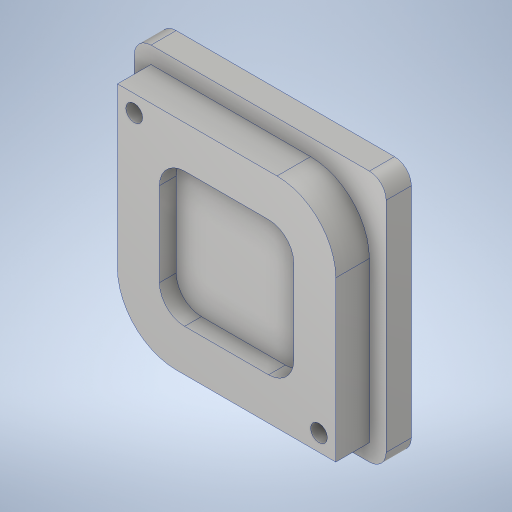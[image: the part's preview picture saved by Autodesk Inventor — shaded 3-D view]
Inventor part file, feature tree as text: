
AUTODESK INVENTOR PART (.ipt)
format: ipt  version: 2024 (Build 280153000, 153)  size: 330,752 bytes
history: native  units: in
note: dims shown in document units (in); Inventor stores cm internally (conversion verified against a paired STEP export)
features: sketch x5, thread x4, extrude x3, fillet x3, hole x2
ambient origin geometry x8: Origin, YZ Plane, XZ Plane, XY Plane, X Axis, Y Axis, Z Axis, Center Point
bodies: Solid1 (feature_tree)
feature tree (17):
  extrude  "Extrusion1"  Depth=3.75in
  extrude  "Extrusion2"  Depth=3.25in
  extrude  "Extrusion3"  Depth=0.5in TaperAngle=0.0deg
  hole  "Hole1"  [1 undecoded]
  hole  "Hole2"  [1 undecoded]
  fillet  "Fillet1"  Radius=0.25in
  fillet  "Fillet3"  Radius=0.25in
  fillet  "Fillet4"  Radius=0.25in
  thread  "Thread1"  [1 undecoded]
  thread  "Thread2"  [1 undecoded]
  thread  "Thread3"  [1 undecoded]
  thread  "Thread4"  [1 undecoded]
  sketch  "Sketch1"  dims[d0=3.75in d1=3.75in]
  sketch  "Sketch2"  dims[d2=0.375in d3=0.0in d4=3.25in]
  sketch  "Sketch3"  dims[d5=3.25in d6=0.5in d7=0.0in]
  sketch  "Sketch4"  dims[d8=2.0in d9=2.0in]
  sketch  "Sketch5"  dims[d10=0.25in d11=0.0in d12=0.25in d13=0.75in d14=0.375in d15=0.25in d16=0.5635in d17=1.0in d18=0.8108in d19=0.25in d20=0.25in d21=0.25in d22=0.25in d23=0.313in d24=0.3389in d25=0.375in d26=0.0625in d27=0.5635in d28=0.625in d29=0.8108in d34=0.25in d36=0.875in d37=2.25in d38=1.125in d39=2.25in d40=1.125in d41=2.25in d42=2.25in d43=1.125in d44=1.125in d45=0.375in d46=0.589in d47=0.0in d48=0.589in d49=0.0in d50=0.589in d51=0.0in d52=0.589in d53=0.0in d30=0.75in d31=0.8108in d32=0.0625in d33=0.75in]
note: 6 required parameter values undecoded (feature->parameter linkage not recoverable at this tier; creation-order binding heuristic only, values carry confidence <= 0.55)
